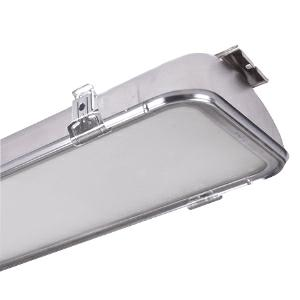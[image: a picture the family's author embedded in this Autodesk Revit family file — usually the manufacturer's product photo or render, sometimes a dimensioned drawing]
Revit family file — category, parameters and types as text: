
# Revit family: 3f_filippi_-_beta_235_93_vs_ampio_3f_filippi_-_52923_-_beta_235_led_932x40_dali_ampio_vs_l1265
name_source: partatom
category: Lighting Fixtures
units: mm (PartAtom-declared; Revit-internal decimal feet)

## family parameters
Cut with Voids When Loaded = No
Host = Face
Light Source = No
Part Type = Normal
Room Calculation Point = No
Round Connector Dimension = Use Diameter
Shared = No

## types (1)
- 3F Filippi - Beta 235 93 VS Ampio (1 x LED, 11449 lm, 80 W, 4000 K)
    Apparent Load = 80 VA
    Approval mark = CE
    CIE Flux Codes = 65 90 98 100 100
    Color Rendering = 80
    Color Temperature = 4000 K
    Control Gear = Electronic transformer
    Default Elevation = 1800 mm
    Description = ILLUMINOTECHNICAL
Luminous efficiency 100% (DLOR 100%, ULOR 0%).
Initial luminous flux of the luminaire 11449 lm.
Wide symmetric distribution.
Installation Interdistance Transv.D = 1.26 x hu - Long.D = 1.32 x hu.
Tabular UGR (CIE 117 - 4H-8H; S=0.25H; 70/50/20): RUG 21.4 - 22.5.
Beam angle: 87° - 92°.
Luminous efficacy 143 lm/W.
Lifetime (L93/B10): 30000 h. (tq+25°C)
Lifetime (L90/B10): 50000 h. (tq+25°C)
Lifetime (L85/B10): 80000 h. (tq+25°C)
Lifetime (L80/B10): 100000 h. (tq+25°C)
Lifetime (L85/B10): 50000 h. (tq+45°C)
Sudden decreased luminous flux after 50000 hours: 0% (C0).
Photobiological safety in compliance with IEC/TR 62778: RG0 risk exempt, (IEC 62471).
In compliance with IEC/EN 62722-2-1 - IEC/EN 62717 standards.

SOURCE
2 linear LED modules 40W/840.
Energy efficiency class (UE 2019/2020 - UE 2019/2015): C.
CIE 13.3 Colour rendering index: CRI >80 (R9 <50%).
IES TM-30 Fidelity Index: Rf = 84 Rg = 95.
CCT nominal colour temperature 4000 K.
Colour initial tolerance (MacAdam): SDCM 3.

MECHANICAL
Housing in AISI 304 stainless steel, pressed in one single piece.
VS moulded anti-glare glass, non-combustible, single-piece perimeter frame in stainless steel.
Oversized gear-tray reflector unit in highly reflective white painted hot-galvanised steel.
Methacrylate (PMMA) lenses with external flat surface.
Stainless steel snap-lock clips for diffuser mounting (safety n° 4 per fixture).
Luminaire with limited surface temperature. - D - (EN 60598-2-24)
Dimensions: 1265x235 mm, height 105 mm. Weight 10.05 kg.
IP65 protection degree.
Mechanical strength to impacts IK09 (10 joule).
Glow-wire test resistance 960°C.

ELECTRICAL
Halogen Free DALI-2 DATI (Parts 251, 252, 253), PUSH-DIM, electronic wiring 230V-50/60Hz, power factor 0.95 at full load, THD <25%, constant output current, class I, 1 driver, 1 DALI addresse.
Power of the luminaire 80 W.
ENEC - CE.
Flicker: <4%.
Luminaire compliant with EN 60598-2-22 for power supply from a centralised emergency system CPSS (Central Power Supply System), not incorporated in the luminaire - high risk areas excluded. The default power and flux are 100% in AC and 15% in DC.
Ambient temperature from -20°C to +45°C.
Temperature class T6 max 85°C.
Quick connection via M25 5P connector with 9-13 mm tightening range.
Relative humidity UR: <85%.

INSTALLATION
Ceiling / Suspended / Wall.
All accessories dedicated to this product are available on the Catalog and on our website www.3F-Filippi.com.

APPLICATIONS
Dry, dusty indoor environments, subject to occasional water splashes.
Any environments except the ones where the luminaire materials are unsuitable.
Industrial environments, warehouses, environments where security locks are required on all clips, e.g. prisons (on request).
Environments in which it is necessary a total protection against falling fragments (eg environments with foodstuffs or machines with moving parts or with extreme temperature changes), use luminaires with laminated glass.
Tempered glass is not immune to falling fragments from harmless and caused by shocks or exceptionally derived from the tempering process.

LIGHT MANAGEMENT
Recommended minimum setting: 10%.
The luminaire, equipped with (DALI-2 DATI) driver, can be controlled manually with 3F Easy Dim technology or automatically/manually with wired or wireless DALI/D2D control systems.
The D2D driver guarantees interoperability with other devices with the same certification by making the following information available:
Device Data (Part 251), Energy Report (Part 252), Diagnosis & Maintenance (Part 253).
In electrical systems without a regulation system (manual or automatic) and DALI bus, a suitable jumper must be made on the DA-DA terminals of the appliance.

WARNING
Fixture not suitable for cold stores with an ambient temperature <0°C and/or relative humidity >85%.
Luminaire designed for disposal/recycling at end-of-life.
Replaceable (LED only) light source by a professional. Replaceable control gear by a professional.
    Height = 105 mm
    Lamp = 1 x LED
    Lamp Light Flux = 11449 lm
    Lamp Power = 80 W
    Lamp count = 1
    Length = 1265 mm
    Lifetime = 50000 h
    Luminous efficacy = 143 lm/W
    Manufacturer = 3F Filippi
    ModVariant = No
    Model = 3F Filippi - 52923 - Beta 235 LED 932x40 DALI AMPIO VS L1265
    Mounting Place = Ceiling
    Mounting Type = Pendant
    Number of Poles = 1
    OnlyDefault = Yes
    Power Factor = 1
    Product Name = 3F Filippi - Beta 235 93 VS Ampio
    Product group = pendant luminaire
    ProductGroupID = 9
    Protection Class = Protection class I
    Protection Degree = IP 65
    RLX_Detail_Level = 1
    RLX_Emergency_Light_Flux = 0 lm
    RLX_Emergency_Type = 0
    RLX_Emergency_Type_DB = No
    RlxData = <blob elided: 85389 chars, md5=0a527844>
    Socket = socket
    Standby Power = 0 W
    System Light Flux = 11449 lm
    System Power = 80 W
    Type Comments = Product without accessories
    Type Image = 3ffilippi_52923.jpg
    URL = http://relux.com
    VarID = ---
    Voltage = 0 V
    Weight = 0.00 kg
    Width = 235 mm

## geometry (parser evidence)
native form markers: Blend x4, Sweep x10
no freeform markers — native parametric forms only
